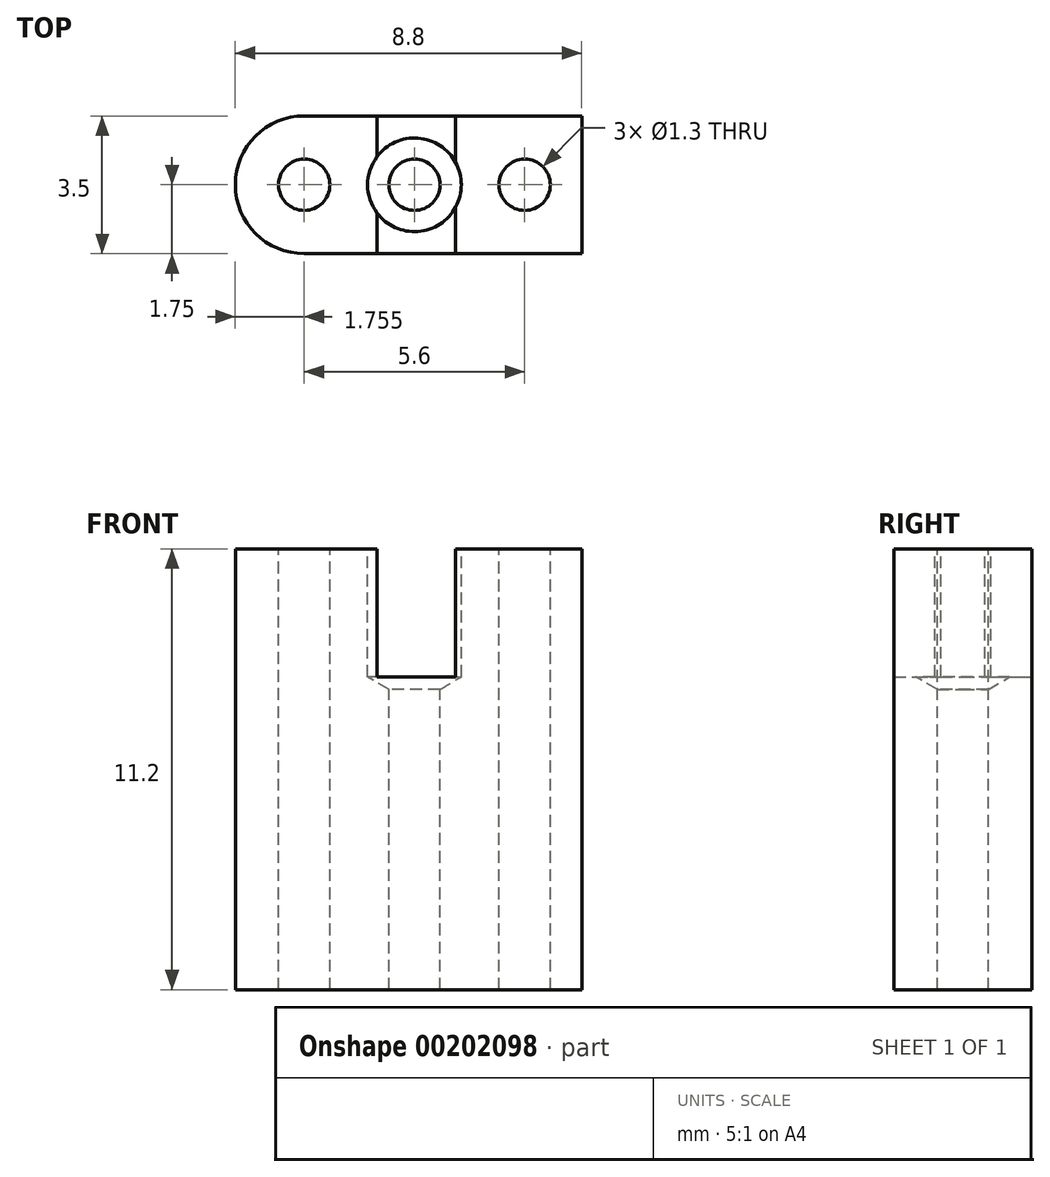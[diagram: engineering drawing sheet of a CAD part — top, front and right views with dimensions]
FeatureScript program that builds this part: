
annotation { "Feature Type Name" : "Feature", "Feature Type Description" : "" }
export const myFeature = defineFeature(function(context is Context, id is Id, definition is map)
    precondition{}
    {
        {
            var Q0;
            Q0=qCreatedBy(makeId("Top.planeOp"),FACE);
            var sketch = newSketch(context, id + "F0", { "sketchPlane" : qUnion([Q0])});
            skLineSegment(sketch, "E0.bottom", {"start": v(3.52, -1.75) * mm, "end": v(-3.53, -1.75) * mm});
            skLineSegment(sketch, "E0.top", {"start": v(3.52, 1.75) * mm, "end": v(-3.53, 1.75) * mm});
            skLineSegment(sketch, "E0.left", {"start": v(3.52, -1.75) * mm, "end": v(3.52, 1.75) * mm});
            skLineSegment(sketch, "E0.right", {"start": v(-3.53, -1.75) * mm, "end": v(-3.53, 1.75) * mm});
            skPoint(sketch, "E0.middle", {"position": v(0, 0) * mm});
            skArc(sketch, "E1", {"start": v(-3.53, 1.75) * mm, "mid": v(-5.28, 0) * mm, "end": v(-3.52, -1.75) * mm});
            skSolve(sketch);
        }
        {
            var Q0;
            Q0=qSketchRegion(id+"F0",true);
            extrude(context, id + "F1", {"entities" : qUnion([Q0]), "depth" : 11.2 * mm});
        }
        {
            var Q0;
            Q0=makeQuery(id+"F1.opExtrude","CAP_FACE",FACE,{"disambiguationData":[OSD([sQuery(id+"F0.wireOp",EDGE,"E0.bottom"),sQuery(id+"F0.wireOp",EDGE,"E0.top"),sQuery(id+"F0.wireOp",EDGE,"E0.left"),sQuery(id+"F0.wireOp",EDGE,"E1")])],"isStart":false});
            var sketch = newSketch(context, id + "F2", { "sketchPlane" : qUnion([Q0])});
            skPoint(sketch, "E2", {"position": v(0, 0) * mm});
            skPoint(sketch, "E3", {"position": v(-0.73, 0) * mm});
            skPoint(sketch, "E4", {"position": v(-3.53, 0) * mm});
            skPoint(sketch, "E5", {"position": v(2.07, 0) * mm});
            skSolve(sketch);
        }
        {
            var Q0;
            Q0=sQuery(id+"F2.wireOp",VERTEX,"E3");
            var Q1;
            Q1=makeQuery(id+"F1.opExtrude","SWEPT_BODY",BODY,{"disambiguationData":[OSD([sQuery(id+"F0.wireOp",EDGE,"E0.bottom"),sQuery(id+"F0.wireOp",EDGE,"E0.top"),sQuery(id+"F0.wireOp",EDGE,"E0.left"),sQuery(id+"F0.wireOp",EDGE,"E1")])]});
            hole(context, id + "F3", {"style" : HoleStyle.SIMPLE, "endStyle" : HoleEndStyle.BLIND, "holeDiameter" : 2.38 * mm, "holeDepth" : 3.25 * mm, "locations" : qUnion([Q0]), "scope" : qUnion([Q1])});
        }
        {
            var Q0;
            Q0=makeQuery(id+"F1.opExtrude","CAP_FACE",FACE,{"disambiguationData":[OSD([sQuery(id+"F0.wireOp",EDGE,"E0.bottom"),sQuery(id+"F0.wireOp",EDGE,"E0.top"),sQuery(id+"F0.wireOp",EDGE,"E0.left"),sQuery(id+"F0.wireOp",EDGE,"E1")])],"isStart":false});
            var sketch = newSketch(context, id + "F4", { "sketchPlane" : qUnion([Q0])});
            skPoint(sketch, "E6", {"position": v(0, 0) * mm});
            skPoint(sketch, "E7", {"position": v(-0.73, 0) * mm});
            skPoint(sketch, "E8", {"position": v(-3.53, 0) * mm});
            skPoint(sketch, "E9", {"position": v(2.07, 0) * mm});
            skSolve(sketch);
        }
        {
            var Q0;
            Q0=sQuery(id+"F4.wireOp",VERTEX,"E8");
            var Q1;
            Q1=sQuery(id+"F4.wireOp",VERTEX,"E7");
            var Q2;
            Q2=sQuery(id+"F4.wireOp",VERTEX,"E9");
            var Q3;
            Q3=makeQuery(id+"F1.opExtrude","SWEPT_BODY",BODY,{"disambiguationData":[OSD([sQuery(id+"F0.wireOp",EDGE,"E0.bottom"),sQuery(id+"F0.wireOp",EDGE,"E0.top"),sQuery(id+"F0.wireOp",EDGE,"E0.left"),sQuery(id+"F0.wireOp",EDGE,"E1")])]});
            hole(context, id + "F5", {"style" : HoleStyle.SIMPLE, "endStyle" : HoleEndStyle.THROUGH, "holeDiameter" : 1.3 * mm, "locations" : qUnion([Q0, Q1, Q2]), "scope" : qUnion([Q3]), "isTappedThrough" : true});
        }
        {
            var Q0;
            Q0=makeQuery(id+"F1.opExtrude","CAP_FACE",FACE,{"disambiguationData":[OSD([sQuery(id+"F0.wireOp",EDGE,"E0.bottom"),sQuery(id+"F0.wireOp",EDGE,"E0.top"),sQuery(id+"F0.wireOp",EDGE,"E0.left"),sQuery(id+"F0.wireOp",EDGE,"E1")])],"isStart":false});
            var sketch = newSketch(context, id + "F6", { "sketchPlane" : qUnion([Q0])});
            skPoint(sketch, "E10", {"position": v(-0.74, 1.19) * mm});
            skPoint(sketch, "E11", {"position": v(-0.74, -1.19) * mm});
            skSolve(sketch);
        }
        {
            var Q0;
            Q0=makeQuery(id+"F6.imprint","IMPRINT",FACE,{"disambiguationData":[TD([[makeQuery(id+"F6.imprint","IMPRINT",EDGE,{"derivedFrom":makeQuery(id+"F1.opExtrude","CAP_EDGE",EDGE,{"disambiguationData":[OSD([sQuery(id+"F0.wireOp",EDGE,"E0.bottom")])],"isStart":false})}),-1.0]])]});
            var sketch = newSketch(context, id + "F7", { "sketchPlane" : qUnion([Q0])});
            skLineSegment(sketch, "E12.bottom", {"start": v(0.32, -1.75) * mm, "end": v(-1.68, -1.75) * mm});
            skLineSegment(sketch, "E12.top", {"start": v(0.32, 1.75) * mm, "end": v(-1.68, 1.75) * mm});
            skLineSegment(sketch, "E12.left", {"start": v(0.32, -1.75) * mm, "end": v(0.32, 1.75) * mm});
            skLineSegment(sketch, "E12.right", {"start": v(-1.68, -1.75) * mm, "end": v(-1.68, 1.75) * mm});
            skPoint(sketch, "E12.middle", {"position": v(-0.68, 0) * mm});
            skSolve(sketch);
        }
        {
            var Q0;
            {var subQ0=sQuery(id+"F7.wireOp",EDGE,"E12.bottom");Q0=makeQuery(id+"F7.imprint","IMPRINT",FACE,{"disambiguationData":[TD([[makeQuery(id+"F7.imprint","IMPRINT",EDGE,{"derivedFrom":subQ0}),-1.0]])]});}
            var Q1;
            {var subQ0=sQuery(id+"F7.wireOp",EDGE,"E12.top");Q1=makeQuery(id+"F7.imprint","IMPRINT",FACE,{"disambiguationData":[TD([[makeQuery(id+"F7.imprint","IMPRINT",EDGE,{"derivedFrom":subQ0}),1.0]])]});}
            extrude(context, id + "F8", {"entities" : qUnion([Q0, Q1]), "operationType" : NewBodyOperationType.REMOVE, "oppositeDirection" : true, "depth" : 3.25 * mm});
        }
    });
